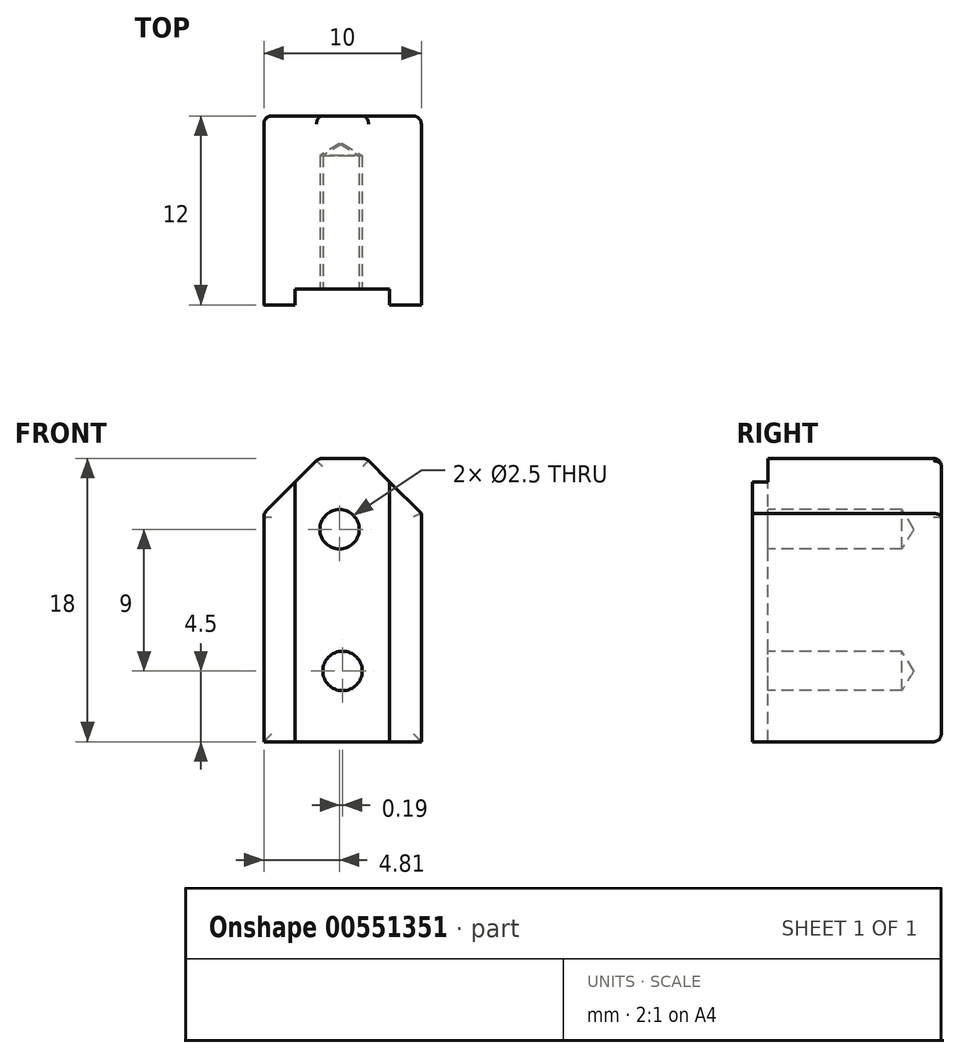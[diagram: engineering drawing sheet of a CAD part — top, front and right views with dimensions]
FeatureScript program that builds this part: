
annotation { "Feature Type Name" : "Feature", "Feature Type Description" : "" }
export const myFeature = defineFeature(function(context is Context, id is Id, definition is map)
    precondition{}
    {
        {
            var Q0;
            Q0=qCreatedBy(makeId("Front.planeOp"),FACE);
            var sketch = newSketch(context, id + "F0", { "sketchPlane" : qUnion([Q0])});
            skLineSegment(sketch, "E0.bottom", {"start": v(0, 0) * mm, "end": v(10, 0) * mm});
            skLineSegment(sketch, "E0.top", {"start": v(3.5, 18) * mm, "end": v(6.5, 18) * mm});
            skLineSegment(sketch, "E0.left", {"start": v(0, 0) * mm, "end": v(0, 14.5) * mm});
            skLineSegment(sketch, "E0.right", {"start": v(10, 0) * mm, "end": v(10, 14.5) * mm});
            skPoint(sketch, "E1", {"position": v(3.5, 18) * mm});
            skPoint(sketch, "E2", {"position": v(0, 14.5) * mm});
            skPoint(sketch, "E3", {"position": v(6.5, 18) * mm});
            skPoint(sketch, "E4", {"position": v(10, 14.5) * mm});
            skLineSegment(sketch, "E5", {"start": v(0, 14.5) * mm, "end": v(3.5, 18) * mm});
            skLineSegment(sketch, "E6", {"start": v(10, 14.5) * mm, "end": v(6.5, 18) * mm});
            skPoint(sketch, "E7.orphan", {"position": v(0, 18) * mm});
            skPoint(sketch, "E8.orphan", {"position": v(10, 18) * mm});
            skSolve(sketch);
        }
        {
            var Q0;
            Q0 = qSketchRegion(id + "F0", true);
            var Q1;
            Q1=makeQuery(id+"F0.imprint","IMPRINT",FACE,{"disambiguationData":[TD([[makeQuery(id+"F0.imprint","IMPRINT",EDGE,{"derivedFrom":sQuery(id+"F0.wireOp",EDGE,"E0.bottom")}),1.0]])]});
            extrude(context, id + "F1", {"entities" : qUnion([Q0, Q1]), "depth" : 12 * mm, "offsetDistance" : 25 * mm});
        }
        {
            var Q0;
            Q0=makeQuery(id+"F1.opExtrude","CAP_FACE",FACE,{"disambiguationData":[OSD([sQuery(id+"F0.wireOp",EDGE,"E0.bottom"),sQuery(id+"F0.wireOp",EDGE,"E0.top"),sQuery(id+"F0.wireOp",EDGE,"E0.left"),sQuery(id+"F0.wireOp",EDGE,"E0.right"),sQuery(id+"F0.wireOp",EDGE,"E5"),sQuery(id+"F0.wireOp",EDGE,"E6")])],"isStart":false});
            var sketch = newSketch(context, id + "F2", { "sketchPlane" : qUnion([Q0])});
            skLineSegment(sketch, "E9.bottom", {"start": v(2, 0) * mm, "end": v(8, 0) * mm});
            skLineSegment(sketch, "E9.top", {"start": v(2, 22.4) * mm, "end": v(8, 22.4) * mm});
            skLineSegment(sketch, "E9.left", {"start": v(2, 0) * mm, "end": v(2, 22.4) * mm});
            skLineSegment(sketch, "E9.right", {"start": v(8, 0) * mm, "end": v(8, 22.4) * mm});
            skSolve(sketch);
        }
        {
            var Q0;
            {var subQ2=sQuery(id+"F2.wireOp",EDGE,"E9.bottom");Q0=makeQuery(id+"F2.imprint","IMPRINT",FACE,{"disambiguationData":[TD([[makeQuery(id+"F2.imprint","IMPRINT",EDGE,{"derivedFrom":subQ2}),1.0]])]});}
            var sketch = newSketch(context, id + "F3", { "sketchPlane" : qUnion([Q0])});
            skSolve(sketch);
        }
        {
            var Q0;
            Q0 = qSketchRegion(id + "F2", true);
            var Q1;
            {var subQ2=sQuery(id+"F2.wireOp",EDGE,"E9.bottom");Q1=makeQuery(id+"F2.imprint","IMPRINT",FACE,{"disambiguationData":[TD([[makeQuery(id+"F2.imprint","IMPRINT",EDGE,{"derivedFrom":subQ2}),1.0]])]});}
            extrude(context, id + "F4", {"entities" : qUnion([Q0, Q1]), "operationType" : NewBodyOperationType.REMOVE, "oppositeDirection" : true, "depth" : 1 * mm, "offsetDistance" : 25 * mm});
        }
        {
            var Q0;
            {var subQ2=sQuery(id+"F2.wireOp",EDGE,"E9.bottom");Q0=makeQuery(id+"F3.imprint","IMPRINT",FACE,{"disambiguationData":[TD([[makeQuery(id+"F3.imprint","IMPRINT",EDGE,{"derivedFrom":makeQuery(id+"F2.imprint","IMPRINT",EDGE,{"derivedFrom":subQ2})}),1.0]])]});}
            var sketch = newSketch(context, id + "F5", { "sketchPlane" : qUnion([Q0])});
            skPoint(sketch, "E10", {"position": v(5, 4.5) * mm});
            skPoint(sketch, "E11", {"position": v(4.8, 13.5) * mm});
            skSolve(sketch);
        }
        {
            var Q0;
            Q0=sQuery(id+"F5.wireOp",VERTEX,"E11");
            var Q1;
            Q1=sQuery(id+"F5.wireOp",VERTEX,"E10");
            var Q2;
            Q2=makeQuery(id+"F1.opExtrude","SWEPT_BODY",BODY,{"disambiguationData":[OSD([sQuery(id+"F0.wireOp",EDGE,"E0.bottom"),sQuery(id+"F0.wireOp",EDGE,"E0.top"),sQuery(id+"F0.wireOp",EDGE,"E0.left"),sQuery(id+"F0.wireOp",EDGE,"E0.right"),sQuery(id+"F0.wireOp",EDGE,"E5"),sQuery(id+"F0.wireOp",EDGE,"E6")])]});
            hole(context, id + "F6", {"style" : HoleStyle.SIMPLE, "endStyle" : HoleEndStyle.BLIND, "standardTappedOrClearance" : lookupTablePath({ "standard" : "ISO", "engagement" : "75%", "pitch" : "0.5 mm", "size" : "M3", "type" : "Tapped" }), "standardBlindInLast" : lookupTablePath({ "standard" : "ISO", "engagement" : "75%", "pitch" : "0.5 mm", "size" : "M3", "type" : "Tapped" }), "holeDiameter" : 2.5 * mm, "showTappedDepth" : true, "holeDepth" : 9.5 * mm, "isTappedThrough" : true, "tappedDepth" : 8 * mm, "tapClearance" : 3, "startFromSketch" : true, "locations" : qUnion([Q0, Q1]), "scope" : qUnion([Q2]), "majorDiameter" : 3 * mm});
        }
        {
            var Q0;
            Q0=makeQuery(id+"F1.opExtrude","CAP_EDGE",EDGE,{"disambiguationData":[OSD([sQuery(id+"F0.wireOp",EDGE,"E0.right")])],"isStart":true});
            var Q1;
            Q1=makeQuery(id+"F1.opExtrude","CAP_EDGE",EDGE,{"disambiguationData":[OSD([sQuery(id+"F0.wireOp",EDGE,"E6")])],"isStart":true});
            var Q2;
            Q2=makeQuery(id+"F1.opExtrude","CAP_EDGE",EDGE,{"disambiguationData":[OSD([sQuery(id+"F0.wireOp",EDGE,"E0.left")])],"isStart":true});
            var Q3;
            Q3=makeQuery(id+"F1.opExtrude","CAP_EDGE",EDGE,{"disambiguationData":[OSD([sQuery(id+"F0.wireOp",EDGE,"E0.bottom")])],"isStart":true});
            fillet(context, id + "F7", {"entities" : qUnion([Q0, Q1, Q2, Q3]), "radius" : .5 * mm, "tangentPropagation" : true, "allowEdgeOverflow" : false});
        }
        {
            var Q0;
            Q0=makeQuery(id+"F1.opExtrude","CAP_EDGE",EDGE,{"disambiguationData":[OSD([sQuery(id+"F0.wireOp",EDGE,"E0.top")])],"isStart":true});
            var Q1;
            Q1=makeQuery(id+"F1.opExtrude","CAP_EDGE",EDGE,{"disambiguationData":[OSD([sQuery(id+"F0.wireOp",EDGE,"E5")])],"isStart":true});
            fillet(context, id + "F8", {"entities" : qUnion([Q0, Q1]), "radius" : .5 * mm, "tangentPropagation" : true, "allowEdgeOverflow" : false});
        }
        {
            var Q0;
            Q0=makeQuery(id+"F1.opExtrude","SWEPT_EDGE",EDGE,{"disambiguationData":[OSD([sQuery(id+"F0.wireOp",EDGE,"E0.top"),sQuery(id+"F0.wireOp",EDGE,"E5")])]});
            fillet(context, id + "F9", {"entities" : qUnion([Q0]), "radius" : .5 * mm, "tangentPropagation" : true, "allowEdgeOverflow" : false});
        }
    });
